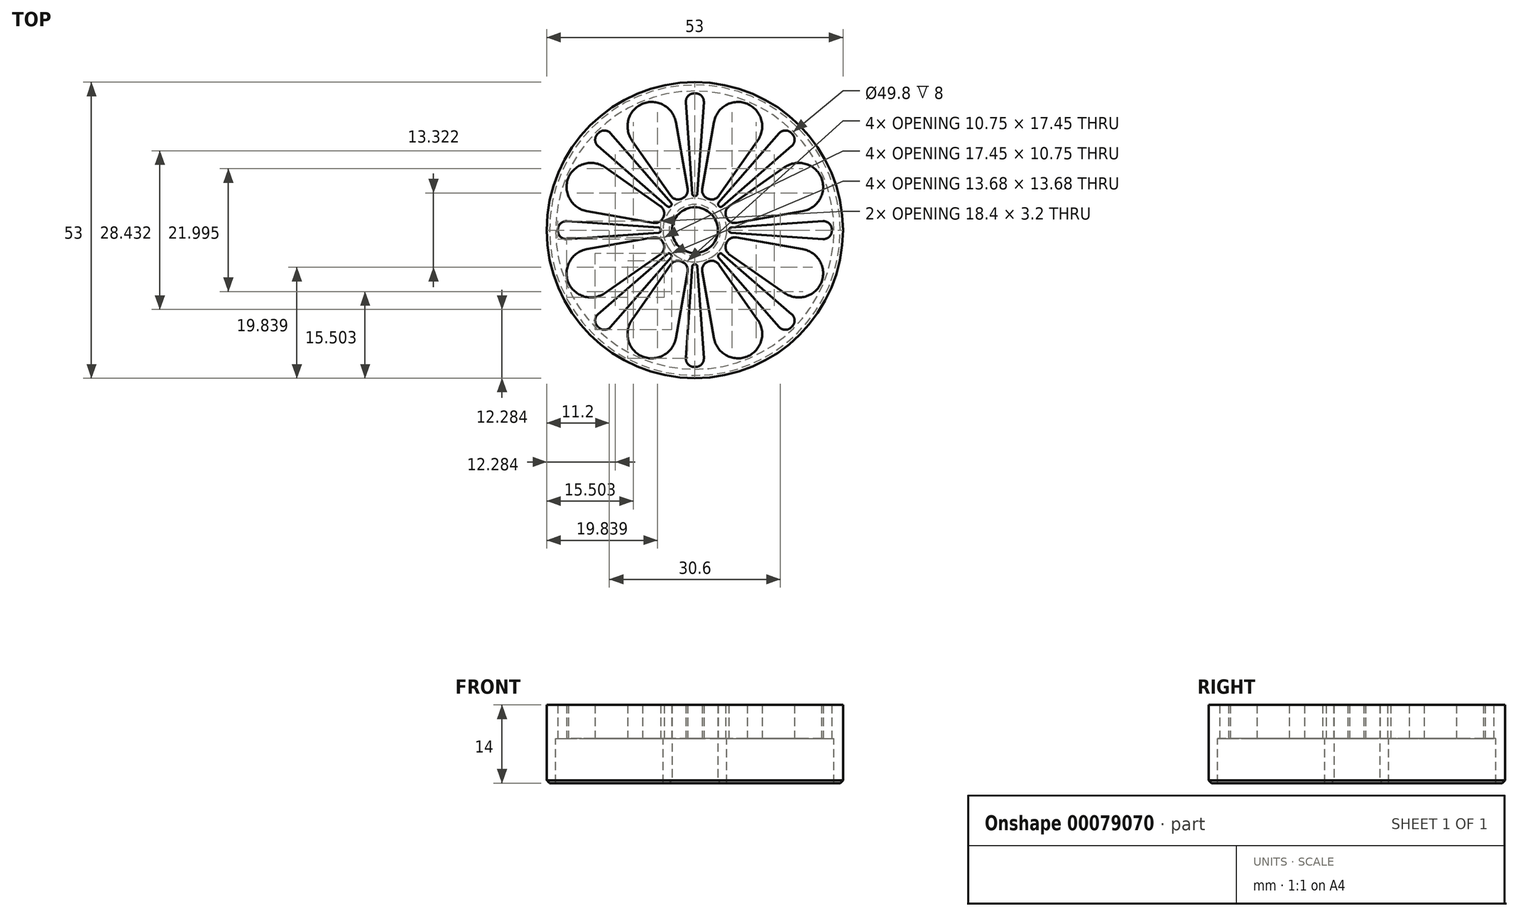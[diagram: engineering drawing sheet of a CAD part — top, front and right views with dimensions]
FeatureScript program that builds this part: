
annotation { "Feature Type Name" : "Feature", "Feature Type Description" : "" }
export const myFeature = defineFeature(function(context is Context, id is Id, definition is map)
    precondition{}
    {
        {
            var Q0;
            Q0=qCreatedBy(makeId("Top.planeOp"),FACE);
            var sketch = newSketch(context, id + "F0", { "sketchPlane" : qUnion([Q0])});
            skCircle(sketch, "E0", {"center": v(0, 0) * mm, "radius": 4.1 * mm});
            skCircle(sketch, "E1", {"center": v(0, 0) * mm, "radius": 26.5 * mm});
            skSolve(sketch);
        }
        {
            var Q0;
            Q0=makeQuery(id+"F0.imprint","IMPRINT",FACE,{"disambiguationData":[TD([[makeQuery(id+"F0.imprint","IMPRINT",EDGE,{"derivedFrom":sQuery(id+"F0.wireOp",EDGE,"E0")}),-1.0]])]});
            extrude(context, id + "F1", {"entities" : qUnion([Q0]), "depth" : 6 * mm});
        }
        {
            var Q0;
            Q0=makeQuery(id+"F1.opExtrude","CAP_FACE",FACE,{"disambiguationData":[OSD([sQuery(id+"F0.wireOp",EDGE,"E0"),sQuery(id+"F0.wireOp",EDGE,"E1")])],"isStart":true});
            var sketch = newSketch(context, id + "F2", { "sketchPlane" : qUnion([Q0])});
            skCircle(sketch, "E2.0", {"center": v(0, 0) * mm, "radius": 6.1 * mm});
            skCircle(sketch, "E3.0", {"center": v(0, 0) * mm, "radius": 24.5 * mm});
            skLineSegment(sketch, "E4", {"start": v(0, 0) * mm, "end": v(0, -26.5) * mm, "construction": true});
            skLineSegment(sketch, "E5", {"start": v(0, 0) * mm, "end": v(-1.7, -24.44) * mm, "construction": true});
            skCircle(sketch, "E6", {"center": v(0, 0) * mm, "radius": 7.1 * mm, "construction": true});
            skCircle(sketch, "E7", {"center": v(0, 0) * mm, "radius": 21.5 * mm, "construction": true});
            skLineSegment(sketch, "E8", {"start": v(0, 0) * mm, "end": v(-4.25, -24.13) * mm, "construction": true});
            skLineSegment(sketch, "E9", {"start": v(0, 0) * mm, "end": v(-1.6, -6.92) * mm, "construction": true});
            skLineSegment(sketch, "E10", {"start": v(-0.43, -6.09) * mm, "end": v(-1.7, -24.44) * mm});
            skLineSegment(sketch, "E11", {"start": v(-4.25, -24.13) * mm, "end": v(-1.06, -6) * mm});
            skLineSegment(sketch, "E12.MirrorCS", {"start": v(4.25, -24.13) * mm, "end": v(1.06, -6) * mm});
            skLineSegment(sketch, "E13.MirrorCS", {"start": v(0.43, -6.09) * mm, "end": v(1.7, -24.44) * mm});
            skLineSegment(sketch, "E14.1.0", {"start": v(4, -4.6) * mm, "end": v(16.07, -18.5) * mm});
            skLineSegment(sketch, "E14.1.1", {"start": v(14.05, -20.07) * mm, "end": v(3.5, -5) * mm});
            skLineSegment(sketch, "E14.1.2", {"start": v(4.6, -4) * mm, "end": v(18.5, -16.07) * mm});
            skLineSegment(sketch, "E14.1.3", {"start": v(20.07, -14.05) * mm, "end": v(5, -3.5) * mm});
            skLineSegment(sketch, "E14.2.0", {"start": v(6.09, -0.43) * mm, "end": v(24.44, -1.7) * mm});
            skLineSegment(sketch, "E14.2.1", {"start": v(24.13, -4.25) * mm, "end": v(6, -1.06) * mm});
            skLineSegment(sketch, "E14.2.2", {"start": v(6.09, 0.43) * mm, "end": v(24.44, 1.7) * mm});
            skLineSegment(sketch, "E14.2.3", {"start": v(24.13, 4.25) * mm, "end": v(6, 1.06) * mm});
            skLineSegment(sketch, "E14.3.0", {"start": v(4.6, 4) * mm, "end": v(18.5, 16.07) * mm});
            skLineSegment(sketch, "E14.3.1", {"start": v(20.07, 14.05) * mm, "end": v(5, 3.5) * mm});
            skLineSegment(sketch, "E14.3.2", {"start": v(4, 4.6) * mm, "end": v(16.07, 18.5) * mm});
            skLineSegment(sketch, "E14.3.3", {"start": v(14.05, 20.07) * mm, "end": v(3.5, 5) * mm});
            skLineSegment(sketch, "E14.4.0", {"start": v(0.43, 6.09) * mm, "end": v(1.7, 24.44) * mm});
            skLineSegment(sketch, "E14.4.1", {"start": v(4.25, 24.13) * mm, "end": v(1.06, 6) * mm});
            skLineSegment(sketch, "E14.4.2", {"start": v(-0.43, 6.09) * mm, "end": v(-1.7, 24.44) * mm});
            skLineSegment(sketch, "E14.4.3", {"start": v(-4.25, 24.13) * mm, "end": v(-1.06, 6) * mm});
            skLineSegment(sketch, "E14.5.0", {"start": v(-4, 4.6) * mm, "end": v(-16.07, 18.5) * mm});
            skLineSegment(sketch, "E14.5.1", {"start": v(-14.05, 20.07) * mm, "end": v(-3.5, 5) * mm});
            skLineSegment(sketch, "E14.5.2", {"start": v(-4.6, 4) * mm, "end": v(-18.5, 16.07) * mm});
            skLineSegment(sketch, "E14.5.3", {"start": v(-20.07, 14.05) * mm, "end": v(-5, 3.5) * mm});
            skLineSegment(sketch, "E14.6.0", {"start": v(-6.09, 0.43) * mm, "end": v(-24.44, 1.7) * mm});
            skLineSegment(sketch, "E14.6.1", {"start": v(-24.13, 4.25) * mm, "end": v(-6, 1.06) * mm});
            skLineSegment(sketch, "E14.6.2", {"start": v(-6.09, -0.43) * mm, "end": v(-24.44, -1.7) * mm});
            skLineSegment(sketch, "E14.6.3", {"start": v(-24.13, -4.25) * mm, "end": v(-6, -1.06) * mm});
            skLineSegment(sketch, "E14.7.0", {"start": v(-4.6, -4) * mm, "end": v(-18.5, -16.07) * mm});
            skLineSegment(sketch, "E14.7.1", {"start": v(-20.07, -14.05) * mm, "end": v(-5, -3.5) * mm});
            skLineSegment(sketch, "E14.7.2", {"start": v(-4, -4.6) * mm, "end": v(-16.07, -18.5) * mm});
            skLineSegment(sketch, "E14.7.3", {"start": v(-14.05, -20.07) * mm, "end": v(-3.5, -5) * mm});
            skSolve(sketch);
        }
        {
            var Q0;
            {var subQ0=sQuery(id+"F2.wireOp",EDGE,"E14.2.3");Q0=makeQuery(id+"F2.imprint","IMPRINT",FACE,{"disambiguationData":[TD([[makeQuery(id+"F2.imprint","IMPRINT",EDGE,{"derivedFrom":subQ0}),-1.0]])]});}
            var Q1;
            {var subQ0=sQuery(id+"F2.wireOp",EDGE,"E14.2.0");Q1=makeQuery(id+"F2.imprint","IMPRINT",FACE,{"disambiguationData":[TD([[makeQuery(id+"F2.imprint","IMPRINT",EDGE,{"derivedFrom":subQ0}),1.0]])]});}
            var Q2;
            {var subQ0=sQuery(id+"F2.wireOp",EDGE,"E14.1.3");Q2=makeQuery(id+"F2.imprint","IMPRINT",FACE,{"disambiguationData":[TD([[makeQuery(id+"F2.imprint","IMPRINT",EDGE,{"derivedFrom":subQ0}),-1.0]])]});}
            var Q3;
            {var subQ0=sQuery(id+"F2.wireOp",EDGE,"E14.1.0");Q3=makeQuery(id+"F2.imprint","IMPRINT",FACE,{"disambiguationData":[TD([[makeQuery(id+"F2.imprint","IMPRINT",EDGE,{"derivedFrom":subQ0}),1.0]])]});}
            var Q4;
            {var subQ0=sQuery(id+"F2.wireOp",EDGE,"E12.MirrorCS");Q4=makeQuery(id+"F2.imprint","IMPRINT",FACE,{"disambiguationData":[TD([[makeQuery(id+"F2.imprint","IMPRINT",EDGE,{"derivedFrom":subQ0}),-1.0]])]});}
            var Q5;
            {var subQ0=sQuery(id+"F2.wireOp",EDGE,"E10");Q5=makeQuery(id+"F2.imprint","IMPRINT",FACE,{"disambiguationData":[TD([[makeQuery(id+"F2.imprint","IMPRINT",EDGE,{"derivedFrom":subQ0}),1.0]])]});}
            var Q6;
            {var subQ0=sQuery(id+"F2.wireOp",EDGE,"E11");Q6=makeQuery(id+"F2.imprint","IMPRINT",FACE,{"disambiguationData":[TD([[makeQuery(id+"F2.imprint","IMPRINT",EDGE,{"derivedFrom":subQ0}),1.0]])]});}
            var Q7;
            {var subQ0=sQuery(id+"F2.wireOp",EDGE,"E14.7.0");Q7=makeQuery(id+"F2.imprint","IMPRINT",FACE,{"disambiguationData":[TD([[makeQuery(id+"F2.imprint","IMPRINT",EDGE,{"derivedFrom":subQ0}),1.0]])]});}
            var Q8;
            {var subQ0=sQuery(id+"F2.wireOp",EDGE,"E14.6.3");Q8=makeQuery(id+"F2.imprint","IMPRINT",FACE,{"disambiguationData":[TD([[makeQuery(id+"F2.imprint","IMPRINT",EDGE,{"derivedFrom":subQ0}),-1.0]])]});}
            var Q9;
            {var subQ0=sQuery(id+"F2.wireOp",EDGE,"E14.6.0");Q9=makeQuery(id+"F2.imprint","IMPRINT",FACE,{"disambiguationData":[TD([[makeQuery(id+"F2.imprint","IMPRINT",EDGE,{"derivedFrom":subQ0}),1.0]])]});}
            var Q10;
            {var subQ0=sQuery(id+"F2.wireOp",EDGE,"E14.5.3");Q10=makeQuery(id+"F2.imprint","IMPRINT",FACE,{"disambiguationData":[TD([[makeQuery(id+"F2.imprint","IMPRINT",EDGE,{"derivedFrom":subQ0}),-1.0]])]});}
            var Q11;
            {var subQ0=sQuery(id+"F2.wireOp",EDGE,"E14.5.0");Q11=makeQuery(id+"F2.imprint","IMPRINT",FACE,{"disambiguationData":[TD([[makeQuery(id+"F2.imprint","IMPRINT",EDGE,{"derivedFrom":subQ0}),1.0]])]});}
            var Q12;
            {var subQ0=sQuery(id+"F2.wireOp",EDGE,"E14.4.3");Q12=makeQuery(id+"F2.imprint","IMPRINT",FACE,{"disambiguationData":[TD([[makeQuery(id+"F2.imprint","IMPRINT",EDGE,{"derivedFrom":subQ0}),-1.0]])]});}
            var Q13;
            {var subQ0=sQuery(id+"F2.wireOp",EDGE,"E14.4.0");Q13=makeQuery(id+"F2.imprint","IMPRINT",FACE,{"disambiguationData":[TD([[makeQuery(id+"F2.imprint","IMPRINT",EDGE,{"derivedFrom":subQ0}),1.0]])]});}
            var Q14;
            {var subQ0=sQuery(id+"F2.wireOp",EDGE,"E14.3.3");Q14=makeQuery(id+"F2.imprint","IMPRINT",FACE,{"disambiguationData":[TD([[makeQuery(id+"F2.imprint","IMPRINT",EDGE,{"derivedFrom":subQ0}),-1.0]])]});}
            var Q15;
            {var subQ0=sQuery(id+"F2.wireOp",EDGE,"E14.3.0");Q15=makeQuery(id+"F2.imprint","IMPRINT",FACE,{"disambiguationData":[TD([[makeQuery(id+"F2.imprint","IMPRINT",EDGE,{"derivedFrom":subQ0}),1.0]])]});}
            extrude(context, id + "F3", {"entities" : qUnion([Q0, Q1, Q2, Q3, Q4, Q5, Q6, Q7, Q8, Q9, Q10, Q11, Q12, Q13, Q14, Q15]), "operationType" : NewBodyOperationType.REMOVE, "endBound" : BoundingType.UP_TO_NEXT, "oppositeDirection" : true, "depth" : 25 * mm});
        }
        {
            var Q0;
            Q0=makeQuery(id+"F3.boolean.opBoolean","COPY",EDGE,{"derivedFrom":makeQuery(id+"F3.opExtrude","SWEPT_EDGE",EDGE,{"disambiguationData":[OSD([sQuery(id+"F2.wireOp",EDGE,"E2.0"),sQuery(id+"F2.wireOp",EDGE,"E14.4.2")])]})});
            var Q1;
            Q1=makeQuery(id+"F3.boolean.opBoolean","COPY",EDGE,{"derivedFrom":makeQuery(id+"F3.opExtrude","SWEPT_EDGE",EDGE,{"disambiguationData":[OSD([sQuery(id+"F2.wireOp",EDGE,"E2.0"),sQuery(id+"F2.wireOp",EDGE,"E14.4.0")])]})});
            var Q2;
            Q2=makeQuery(id+"F3.boolean.opBoolean","COPY",EDGE,{"derivedFrom":makeQuery(id+"F3.opExtrude","SWEPT_EDGE",EDGE,{"disambiguationData":[OSD([sQuery(id+"F2.wireOp",EDGE,"E2.0"),sQuery(id+"F2.wireOp",EDGE,"E14.3.2")])]})});
            var Q3;
            Q3=makeQuery(id+"F3.boolean.opBoolean","COPY",EDGE,{"derivedFrom":makeQuery(id+"F3.opExtrude","SWEPT_EDGE",EDGE,{"disambiguationData":[OSD([sQuery(id+"F2.wireOp",EDGE,"E2.0"),sQuery(id+"F2.wireOp",EDGE,"E14.3.0")])]})});
            var Q4;
            Q4=makeQuery(id+"F3.boolean.opBoolean","COPY",EDGE,{"derivedFrom":makeQuery(id+"F3.opExtrude","SWEPT_EDGE",EDGE,{"disambiguationData":[OSD([sQuery(id+"F2.wireOp",EDGE,"E2.0"),sQuery(id+"F2.wireOp",EDGE,"E14.2.2")])]})});
            var Q5;
            Q5=makeQuery(id+"F3.boolean.opBoolean","COPY",EDGE,{"derivedFrom":makeQuery(id+"F3.opExtrude","SWEPT_EDGE",EDGE,{"disambiguationData":[OSD([sQuery(id+"F2.wireOp",EDGE,"E2.0"),sQuery(id+"F2.wireOp",EDGE,"E14.2.0")])]})});
            var Q6;
            Q6=makeQuery(id+"F3.boolean.opBoolean","COPY",EDGE,{"derivedFrom":makeQuery(id+"F3.opExtrude","SWEPT_EDGE",EDGE,{"disambiguationData":[OSD([sQuery(id+"F2.wireOp",EDGE,"E2.0"),sQuery(id+"F2.wireOp",EDGE,"E14.1.2")])]})});
            var Q7;
            Q7=makeQuery(id+"F3.boolean.opBoolean","COPY",EDGE,{"derivedFrom":makeQuery(id+"F3.opExtrude","SWEPT_EDGE",EDGE,{"disambiguationData":[OSD([sQuery(id+"F2.wireOp",EDGE,"E2.0"),sQuery(id+"F2.wireOp",EDGE,"E14.1.0")])]})});
            var Q8;
            Q8=makeQuery(id+"F3.boolean.opBoolean","COPY",EDGE,{"derivedFrom":makeQuery(id+"F3.opExtrude","SWEPT_EDGE",EDGE,{"disambiguationData":[OSD([sQuery(id+"F2.wireOp",EDGE,"E2.0"),sQuery(id+"F2.wireOp",EDGE,"E13.MirrorCS")])]})});
            var Q9;
            Q9=makeQuery(id+"F3.boolean.opBoolean","COPY",EDGE,{"derivedFrom":makeQuery(id+"F3.opExtrude","SWEPT_EDGE",EDGE,{"disambiguationData":[OSD([sQuery(id+"F2.wireOp",EDGE,"E2.0"),sQuery(id+"F2.wireOp",EDGE,"E10")])]})});
            var Q10;
            Q10=makeQuery(id+"F3.boolean.opBoolean","COPY",EDGE,{"derivedFrom":makeQuery(id+"F3.opExtrude","SWEPT_EDGE",EDGE,{"disambiguationData":[OSD([sQuery(id+"F2.wireOp",EDGE,"E2.0"),sQuery(id+"F2.wireOp",EDGE,"E14.7.2")])]})});
            var Q11;
            Q11=makeQuery(id+"F3.boolean.opBoolean","COPY",EDGE,{"derivedFrom":makeQuery(id+"F3.opExtrude","SWEPT_EDGE",EDGE,{"disambiguationData":[OSD([sQuery(id+"F2.wireOp",EDGE,"E2.0"),sQuery(id+"F2.wireOp",EDGE,"E14.7.0")])]})});
            var Q12;
            Q12=makeQuery(id+"F3.boolean.opBoolean","COPY",EDGE,{"derivedFrom":makeQuery(id+"F3.opExtrude","SWEPT_EDGE",EDGE,{"disambiguationData":[OSD([sQuery(id+"F2.wireOp",EDGE,"E2.0"),sQuery(id+"F2.wireOp",EDGE,"E14.6.0")])]})});
            var Q13;
            Q13=makeQuery(id+"F3.boolean.opBoolean","COPY",EDGE,{"derivedFrom":makeQuery(id+"F3.opExtrude","SWEPT_EDGE",EDGE,{"disambiguationData":[OSD([sQuery(id+"F2.wireOp",EDGE,"E2.0"),sQuery(id+"F2.wireOp",EDGE,"E14.6.2")])]})});
            var Q14;
            Q14=makeQuery(id+"F3.boolean.opBoolean","COPY",EDGE,{"derivedFrom":makeQuery(id+"F3.opExtrude","SWEPT_EDGE",EDGE,{"disambiguationData":[OSD([sQuery(id+"F2.wireOp",EDGE,"E2.0"),sQuery(id+"F2.wireOp",EDGE,"E14.5.0")])]})});
            var Q15;
            Q15=makeQuery(id+"F3.boolean.opBoolean","COPY",EDGE,{"derivedFrom":makeQuery(id+"F3.opExtrude","SWEPT_EDGE",EDGE,{"disambiguationData":[OSD([sQuery(id+"F2.wireOp",EDGE,"E2.0"),sQuery(id+"F2.wireOp",EDGE,"E14.5.2")])]})});
            fillet(context, id + "F4", {"entities" : qUnion([Q0, Q1, Q2, Q3, Q4, Q5, Q6, Q7, Q8, Q9, Q10, Q11, Q12, Q13, Q14, Q15]), "radius" : 0.4 * mm, "tangentPropagation" : true, "allowEdgeOverflow" : false});
        }
        {
            var Q0;
            Q0=makeQuery(id+"F3.boolean.opBoolean","COPY",EDGE,{"derivedFrom":makeQuery(id+"F3.opExtrude","SWEPT_EDGE",EDGE,{"disambiguationData":[OSD([sQuery(id+"F2.wireOp",EDGE,"E2.0"),sQuery(id+"F2.wireOp",EDGE,"E14.6.3")])]})});
            var Q1;
            Q1=makeQuery(id+"F3.boolean.opBoolean","COPY",EDGE,{"derivedFrom":makeQuery(id+"F3.opExtrude","SWEPT_EDGE",EDGE,{"disambiguationData":[OSD([sQuery(id+"F2.wireOp",EDGE,"E2.0"),sQuery(id+"F2.wireOp",EDGE,"E14.7.1")])]})});
            var Q2;
            Q2=makeQuery(id+"F3.boolean.opBoolean","COPY",EDGE,{"derivedFrom":makeQuery(id+"F3.opExtrude","SWEPT_EDGE",EDGE,{"disambiguationData":[OSD([sQuery(id+"F2.wireOp",EDGE,"E2.0"),sQuery(id+"F2.wireOp",EDGE,"E14.7.3")])]})});
            var Q3;
            Q3=makeQuery(id+"F3.boolean.opBoolean","COPY",EDGE,{"derivedFrom":makeQuery(id+"F3.opExtrude","SWEPT_EDGE",EDGE,{"disambiguationData":[OSD([sQuery(id+"F2.wireOp",EDGE,"E2.0"),sQuery(id+"F2.wireOp",EDGE,"E11")])]})});
            var Q4;
            Q4=makeQuery(id+"F3.boolean.opBoolean","COPY",EDGE,{"derivedFrom":makeQuery(id+"F3.opExtrude","SWEPT_EDGE",EDGE,{"disambiguationData":[OSD([sQuery(id+"F2.wireOp",EDGE,"E2.0"),sQuery(id+"F2.wireOp",EDGE,"E12.MirrorCS")])]})});
            var Q5;
            Q5=makeQuery(id+"F3.boolean.opBoolean","COPY",EDGE,{"derivedFrom":makeQuery(id+"F3.opExtrude","SWEPT_EDGE",EDGE,{"disambiguationData":[OSD([sQuery(id+"F2.wireOp",EDGE,"E2.0"),sQuery(id+"F2.wireOp",EDGE,"E14.1.1")])]})});
            var Q6;
            Q6=makeQuery(id+"F3.boolean.opBoolean","COPY",EDGE,{"derivedFrom":makeQuery(id+"F3.opExtrude","SWEPT_EDGE",EDGE,{"disambiguationData":[OSD([sQuery(id+"F2.wireOp",EDGE,"E2.0"),sQuery(id+"F2.wireOp",EDGE,"E14.1.3")])]})});
            var Q7;
            Q7=makeQuery(id+"F3.boolean.opBoolean","COPY",EDGE,{"derivedFrom":makeQuery(id+"F3.opExtrude","SWEPT_EDGE",EDGE,{"disambiguationData":[OSD([sQuery(id+"F2.wireOp",EDGE,"E2.0"),sQuery(id+"F2.wireOp",EDGE,"E14.2.1")])]})});
            var Q8;
            Q8=makeQuery(id+"F3.boolean.opBoolean","COPY",EDGE,{"derivedFrom":makeQuery(id+"F3.opExtrude","SWEPT_EDGE",EDGE,{"disambiguationData":[OSD([sQuery(id+"F2.wireOp",EDGE,"E2.0"),sQuery(id+"F2.wireOp",EDGE,"E14.2.3")])]})});
            var Q9;
            Q9=makeQuery(id+"F3.boolean.opBoolean","COPY",EDGE,{"derivedFrom":makeQuery(id+"F3.opExtrude","SWEPT_EDGE",EDGE,{"disambiguationData":[OSD([sQuery(id+"F2.wireOp",EDGE,"E2.0"),sQuery(id+"F2.wireOp",EDGE,"E14.3.1")])]})});
            var Q10;
            Q10=makeQuery(id+"F3.boolean.opBoolean","COPY",EDGE,{"derivedFrom":makeQuery(id+"F3.opExtrude","SWEPT_EDGE",EDGE,{"disambiguationData":[OSD([sQuery(id+"F2.wireOp",EDGE,"E2.0"),sQuery(id+"F2.wireOp",EDGE,"E14.3.3")])]})});
            var Q11;
            Q11=makeQuery(id+"F3.boolean.opBoolean","COPY",EDGE,{"derivedFrom":makeQuery(id+"F3.opExtrude","SWEPT_EDGE",EDGE,{"disambiguationData":[OSD([sQuery(id+"F2.wireOp",EDGE,"E2.0"),sQuery(id+"F2.wireOp",EDGE,"E14.4.1")])]})});
            var Q12;
            Q12=makeQuery(id+"F3.boolean.opBoolean","COPY",EDGE,{"derivedFrom":makeQuery(id+"F3.opExtrude","SWEPT_EDGE",EDGE,{"disambiguationData":[OSD([sQuery(id+"F2.wireOp",EDGE,"E2.0"),sQuery(id+"F2.wireOp",EDGE,"E14.4.3")])]})});
            var Q13;
            Q13=makeQuery(id+"F3.boolean.opBoolean","COPY",EDGE,{"derivedFrom":makeQuery(id+"F3.opExtrude","SWEPT_EDGE",EDGE,{"disambiguationData":[OSD([sQuery(id+"F2.wireOp",EDGE,"E2.0"),sQuery(id+"F2.wireOp",EDGE,"E14.5.1")])]})});
            var Q14;
            Q14=makeQuery(id+"F3.boolean.opBoolean","COPY",EDGE,{"derivedFrom":makeQuery(id+"F3.opExtrude","SWEPT_EDGE",EDGE,{"disambiguationData":[OSD([sQuery(id+"F2.wireOp",EDGE,"E2.0"),sQuery(id+"F2.wireOp",EDGE,"E14.5.3")])]})});
            var Q15;
            Q15=makeQuery(id+"F3.boolean.opBoolean","COPY",EDGE,{"derivedFrom":makeQuery(id+"F3.opExtrude","SWEPT_EDGE",EDGE,{"disambiguationData":[OSD([sQuery(id+"F2.wireOp",EDGE,"E2.0"),sQuery(id+"F2.wireOp",EDGE,"E14.6.1")])]})});
            fillet(context, id + "F5", {"entities" : qUnion([Q0, Q1, Q2, Q3, Q4, Q5, Q6, Q7, Q8, Q9, Q10, Q11, Q12, Q13, Q14, Q15]), "radius" : 1.6 * mm, "tangentPropagation" : true, "allowEdgeOverflow" : false});
        }
        {
            var Q0;
            Q0=makeQuery(id+"F3.boolean.opBoolean","COPY",EDGE,{"derivedFrom":makeQuery(id+"F3.opExtrude","SWEPT_EDGE",EDGE,{"disambiguationData":[OSD([sQuery(id+"F2.wireOp",EDGE,"E3.0"),sQuery(id+"F2.wireOp",EDGE,"E14.3.2")])]})});
            var Q1;
            Q1=makeQuery(id+"F3.boolean.opBoolean","COPY",EDGE,{"derivedFrom":makeQuery(id+"F3.opExtrude","SWEPT_EDGE",EDGE,{"disambiguationData":[OSD([sQuery(id+"F2.wireOp",EDGE,"E3.0"),sQuery(id+"F2.wireOp",EDGE,"E14.3.0")])]})});
            var Q2;
            Q2=makeQuery(id+"F3.boolean.opBoolean","COPY",EDGE,{"derivedFrom":makeQuery(id+"F3.opExtrude","SWEPT_EDGE",EDGE,{"disambiguationData":[OSD([sQuery(id+"F2.wireOp",EDGE,"E3.0"),sQuery(id+"F2.wireOp",EDGE,"E14.2.2")])]})});
            var Q3;
            Q3=makeQuery(id+"F3.boolean.opBoolean","COPY",EDGE,{"derivedFrom":makeQuery(id+"F3.opExtrude","SWEPT_EDGE",EDGE,{"disambiguationData":[OSD([sQuery(id+"F2.wireOp",EDGE,"E3.0"),sQuery(id+"F2.wireOp",EDGE,"E14.2.0")])]})});
            var Q4;
            Q4=makeQuery(id+"F3.boolean.opBoolean","COPY",EDGE,{"derivedFrom":makeQuery(id+"F3.opExtrude","SWEPT_EDGE",EDGE,{"disambiguationData":[OSD([sQuery(id+"F2.wireOp",EDGE,"E3.0"),sQuery(id+"F2.wireOp",EDGE,"E14.1.2")])]})});
            var Q5;
            Q5=makeQuery(id+"F3.boolean.opBoolean","COPY",EDGE,{"derivedFrom":makeQuery(id+"F3.opExtrude","SWEPT_EDGE",EDGE,{"disambiguationData":[OSD([sQuery(id+"F2.wireOp",EDGE,"E3.0"),sQuery(id+"F2.wireOp",EDGE,"E13.MirrorCS")])]})});
            var Q6;
            Q6=makeQuery(id+"F3.boolean.opBoolean","COPY",EDGE,{"derivedFrom":makeQuery(id+"F3.opExtrude","SWEPT_EDGE",EDGE,{"disambiguationData":[OSD([sQuery(id+"F2.wireOp",EDGE,"E3.0"),sQuery(id+"F2.wireOp",EDGE,"E14.1.0")])]})});
            var Q7;
            Q7=makeQuery(id+"F3.boolean.opBoolean","COPY",EDGE,{"derivedFrom":makeQuery(id+"F3.opExtrude","SWEPT_EDGE",EDGE,{"disambiguationData":[OSD([sQuery(id+"F2.wireOp",EDGE,"E3.0"),sQuery(id+"F2.wireOp",EDGE,"E10")])]})});
            var Q8;
            Q8=makeQuery(id+"F3.boolean.opBoolean","COPY",EDGE,{"derivedFrom":makeQuery(id+"F3.opExtrude","SWEPT_EDGE",EDGE,{"disambiguationData":[OSD([sQuery(id+"F2.wireOp",EDGE,"E3.0"),sQuery(id+"F2.wireOp",EDGE,"E14.7.2")])]})});
            var Q9;
            Q9=makeQuery(id+"F3.boolean.opBoolean","COPY",EDGE,{"derivedFrom":makeQuery(id+"F3.opExtrude","SWEPT_EDGE",EDGE,{"disambiguationData":[OSD([sQuery(id+"F2.wireOp",EDGE,"E3.0"),sQuery(id+"F2.wireOp",EDGE,"E14.7.0")])]})});
            var Q10;
            Q10=makeQuery(id+"F3.boolean.opBoolean","COPY",EDGE,{"derivedFrom":makeQuery(id+"F3.opExtrude","SWEPT_EDGE",EDGE,{"disambiguationData":[OSD([sQuery(id+"F2.wireOp",EDGE,"E3.0"),sQuery(id+"F2.wireOp",EDGE,"E14.6.2")])]})});
            var Q11;
            Q11=makeQuery(id+"F3.boolean.opBoolean","COPY",EDGE,{"derivedFrom":makeQuery(id+"F3.opExtrude","SWEPT_EDGE",EDGE,{"disambiguationData":[OSD([sQuery(id+"F2.wireOp",EDGE,"E3.0"),sQuery(id+"F2.wireOp",EDGE,"E14.6.0")])]})});
            var Q12;
            Q12=makeQuery(id+"F3.boolean.opBoolean","COPY",EDGE,{"derivedFrom":makeQuery(id+"F3.opExtrude","SWEPT_EDGE",EDGE,{"disambiguationData":[OSD([sQuery(id+"F2.wireOp",EDGE,"E3.0"),sQuery(id+"F2.wireOp",EDGE,"E14.5.0")])]})});
            var Q13;
            Q13=makeQuery(id+"F3.boolean.opBoolean","COPY",EDGE,{"derivedFrom":makeQuery(id+"F3.opExtrude","SWEPT_EDGE",EDGE,{"disambiguationData":[OSD([sQuery(id+"F2.wireOp",EDGE,"E3.0"),sQuery(id+"F2.wireOp",EDGE,"E14.5.2")])]})});
            var Q14;
            Q14=makeQuery(id+"F3.boolean.opBoolean","COPY",EDGE,{"derivedFrom":makeQuery(id+"F3.opExtrude","SWEPT_EDGE",EDGE,{"disambiguationData":[OSD([sQuery(id+"F2.wireOp",EDGE,"E3.0"),sQuery(id+"F2.wireOp",EDGE,"E14.4.2")])]})});
            var Q15;
            Q15=makeQuery(id+"F3.boolean.opBoolean","COPY",EDGE,{"derivedFrom":makeQuery(id+"F3.opExtrude","SWEPT_EDGE",EDGE,{"disambiguationData":[OSD([sQuery(id+"F2.wireOp",EDGE,"E3.0"),sQuery(id+"F2.wireOp",EDGE,"E14.4.0")])]})});
            fillet(context, id + "F6", {"entities" : qUnion([Q0, Q1, Q2, Q3, Q4, Q5, Q6, Q7, Q8, Q9, Q10, Q11, Q12, Q13, Q14, Q15]), "radius" : 1.5 * mm, "tangentPropagation" : true, "allowEdgeOverflow" : false});
        }
        {
            var Q0;
            Q0=makeQuery(id+"F3.boolean.opBoolean","COPY",EDGE,{"derivedFrom":makeQuery(id+"F3.opExtrude","SWEPT_EDGE",EDGE,{"disambiguationData":[OSD([sQuery(id+"F2.wireOp",EDGE,"E3.0"),sQuery(id+"F2.wireOp",EDGE,"E14.2.1")])]})});
            var Q1;
            Q1=makeQuery(id+"F3.boolean.opBoolean","COPY",EDGE,{"derivedFrom":makeQuery(id+"F3.opExtrude","SWEPT_EDGE",EDGE,{"disambiguationData":[OSD([sQuery(id+"F2.wireOp",EDGE,"E3.0"),sQuery(id+"F2.wireOp",EDGE,"E14.1.3")])]})});
            var Q2;
            Q2=makeQuery(id+"F3.boolean.opBoolean","COPY",EDGE,{"derivedFrom":makeQuery(id+"F3.opExtrude","SWEPT_EDGE",EDGE,{"disambiguationData":[OSD([sQuery(id+"F2.wireOp",EDGE,"E3.0"),sQuery(id+"F2.wireOp",EDGE,"E14.1.1")])]})});
            var Q3;
            Q3=makeQuery(id+"F3.boolean.opBoolean","COPY",EDGE,{"derivedFrom":makeQuery(id+"F3.opExtrude","SWEPT_EDGE",EDGE,{"disambiguationData":[OSD([sQuery(id+"F2.wireOp",EDGE,"E3.0"),sQuery(id+"F2.wireOp",EDGE,"E12.MirrorCS")])]})});
            var Q4;
            Q4=makeQuery(id+"F3.boolean.opBoolean","COPY",EDGE,{"derivedFrom":makeQuery(id+"F3.opExtrude","SWEPT_EDGE",EDGE,{"disambiguationData":[OSD([sQuery(id+"F2.wireOp",EDGE,"E3.0"),sQuery(id+"F2.wireOp",EDGE,"E11")])]})});
            var Q5;
            Q5=makeQuery(id+"F3.boolean.opBoolean","COPY",EDGE,{"derivedFrom":makeQuery(id+"F3.opExtrude","SWEPT_EDGE",EDGE,{"disambiguationData":[OSD([sQuery(id+"F2.wireOp",EDGE,"E3.0"),sQuery(id+"F2.wireOp",EDGE,"E14.7.3")])]})});
            var Q6;
            Q6=makeQuery(id+"F3.boolean.opBoolean","COPY",EDGE,{"derivedFrom":makeQuery(id+"F3.opExtrude","SWEPT_EDGE",EDGE,{"disambiguationData":[OSD([sQuery(id+"F2.wireOp",EDGE,"E3.0"),sQuery(id+"F2.wireOp",EDGE,"E14.7.1")])]})});
            var Q7;
            Q7=makeQuery(id+"F3.boolean.opBoolean","COPY",EDGE,{"derivedFrom":makeQuery(id+"F3.opExtrude","SWEPT_EDGE",EDGE,{"disambiguationData":[OSD([sQuery(id+"F2.wireOp",EDGE,"E3.0"),sQuery(id+"F2.wireOp",EDGE,"E14.6.3")])]})});
            var Q8;
            Q8=makeQuery(id+"F3.boolean.opBoolean","COPY",EDGE,{"derivedFrom":makeQuery(id+"F3.opExtrude","SWEPT_EDGE",EDGE,{"disambiguationData":[OSD([sQuery(id+"F2.wireOp",EDGE,"E3.0"),sQuery(id+"F2.wireOp",EDGE,"E14.6.1")])]})});
            var Q9;
            Q9=makeQuery(id+"F3.boolean.opBoolean","COPY",EDGE,{"derivedFrom":makeQuery(id+"F3.opExtrude","SWEPT_EDGE",EDGE,{"disambiguationData":[OSD([sQuery(id+"F2.wireOp",EDGE,"E3.0"),sQuery(id+"F2.wireOp",EDGE,"E14.5.3")])]})});
            var Q10;
            Q10=makeQuery(id+"F3.boolean.opBoolean","COPY",EDGE,{"derivedFrom":makeQuery(id+"F3.opExtrude","SWEPT_EDGE",EDGE,{"disambiguationData":[OSD([sQuery(id+"F2.wireOp",EDGE,"E3.0"),sQuery(id+"F2.wireOp",EDGE,"E14.5.1")])]})});
            var Q11;
            Q11=makeQuery(id+"F3.boolean.opBoolean","COPY",EDGE,{"derivedFrom":makeQuery(id+"F3.opExtrude","SWEPT_EDGE",EDGE,{"disambiguationData":[OSD([sQuery(id+"F2.wireOp",EDGE,"E3.0"),sQuery(id+"F2.wireOp",EDGE,"E14.4.3")])]})});
            var Q12;
            Q12=makeQuery(id+"F3.boolean.opBoolean","COPY",EDGE,{"derivedFrom":makeQuery(id+"F3.opExtrude","SWEPT_EDGE",EDGE,{"disambiguationData":[OSD([sQuery(id+"F2.wireOp",EDGE,"E3.0"),sQuery(id+"F2.wireOp",EDGE,"E14.4.1")])]})});
            var Q13;
            Q13=makeQuery(id+"F3.boolean.opBoolean","COPY",EDGE,{"derivedFrom":makeQuery(id+"F3.opExtrude","SWEPT_EDGE",EDGE,{"disambiguationData":[OSD([sQuery(id+"F2.wireOp",EDGE,"E3.0"),sQuery(id+"F2.wireOp",EDGE,"E14.3.3")])]})});
            var Q14;
            Q14=makeQuery(id+"F3.boolean.opBoolean","COPY",EDGE,{"derivedFrom":makeQuery(id+"F3.opExtrude","SWEPT_EDGE",EDGE,{"disambiguationData":[OSD([sQuery(id+"F2.wireOp",EDGE,"E3.0"),sQuery(id+"F2.wireOp",EDGE,"E14.3.1")])]})});
            var Q15;
            Q15=makeQuery(id+"F3.boolean.opBoolean","COPY",EDGE,{"derivedFrom":makeQuery(id+"F3.opExtrude","SWEPT_EDGE",EDGE,{"disambiguationData":[OSD([sQuery(id+"F2.wireOp",EDGE,"E3.0"),sQuery(id+"F2.wireOp",EDGE,"E14.2.3")])]})});
            fillet(context, id + "F7", {"entities" : qUnion([Q0, Q1, Q2, Q3, Q4, Q5, Q6, Q7, Q8, Q9, Q10, Q11, Q12, Q13, Q14, Q15]), "radius" : 4.4 * mm, "tangentPropagation" : true, "allowEdgeOverflow" : false});
        }
        {
            var Q0;
            Q0=makeQuery(id+"F1.opExtrude","CAP_FACE",FACE,{"disambiguationData":[OSD([sQuery(id+"F0.wireOp",EDGE,"E0"),sQuery(id+"F0.wireOp",EDGE,"E1")])],"isStart":true});
            var sketch = newSketch(context, id + "F8", { "sketchPlane" : qUnion([Q0])});
            skCircle(sketch, "E15.0", {"center": v(0, 0) * mm, "radius": 24.9 * mm});
            skCircle(sketch, "E16.0", {"center": v(0, 0) * mm, "radius": 5.7 * mm});
            skSolve(sketch);
        }
        {
            var Q0;
            Q0=makeQuery(id+"F8.imprint","IMPRINT",FACE,{"disambiguationData":[TD([[makeQuery(id+"F8.imprint","IMPRINT",EDGE,{"derivedFrom":sQuery(id+"F8.wireOp",EDGE,"E15.0")}),-1.0]])]});
            var Q1;
            Q1=makeQuery(id+"F8.imprint","IMPRINT",FACE,{"disambiguationData":[TD([[makeQuery(id+"F8.imprint","IMPRINT",EDGE,{"derivedFrom":sQuery(id+"F8.wireOp",EDGE,"E16.0")}),1.0]])]});
            extrude(context, id + "F9", {"entities" : qUnion([Q0, Q1]), "operationType" : NewBodyOperationType.ADD, "depth" : 8 * mm});
        }
        {
            var Q0;
            Q0=makeQuery(id+"F9.opExtrude","CAP_EDGE",EDGE,{"disambiguationData":[OSD([sQuery(id+"F0.wireOp",EDGE,"E1")])],"isStart":false});
            var Q1;
            Q1=makeQuery(id+"F9.opExtrude","CAP_EDGE",EDGE,{"disambiguationData":[OSD([sQuery(id+"F0.wireOp",EDGE,"E0")])],"isStart":false});
            chamfer(context, id + "F10", {"entities" : qUnion([Q0, Q1]), "width" : 0.5 * mm, "tangentPropagation" : true});
        }
    });
